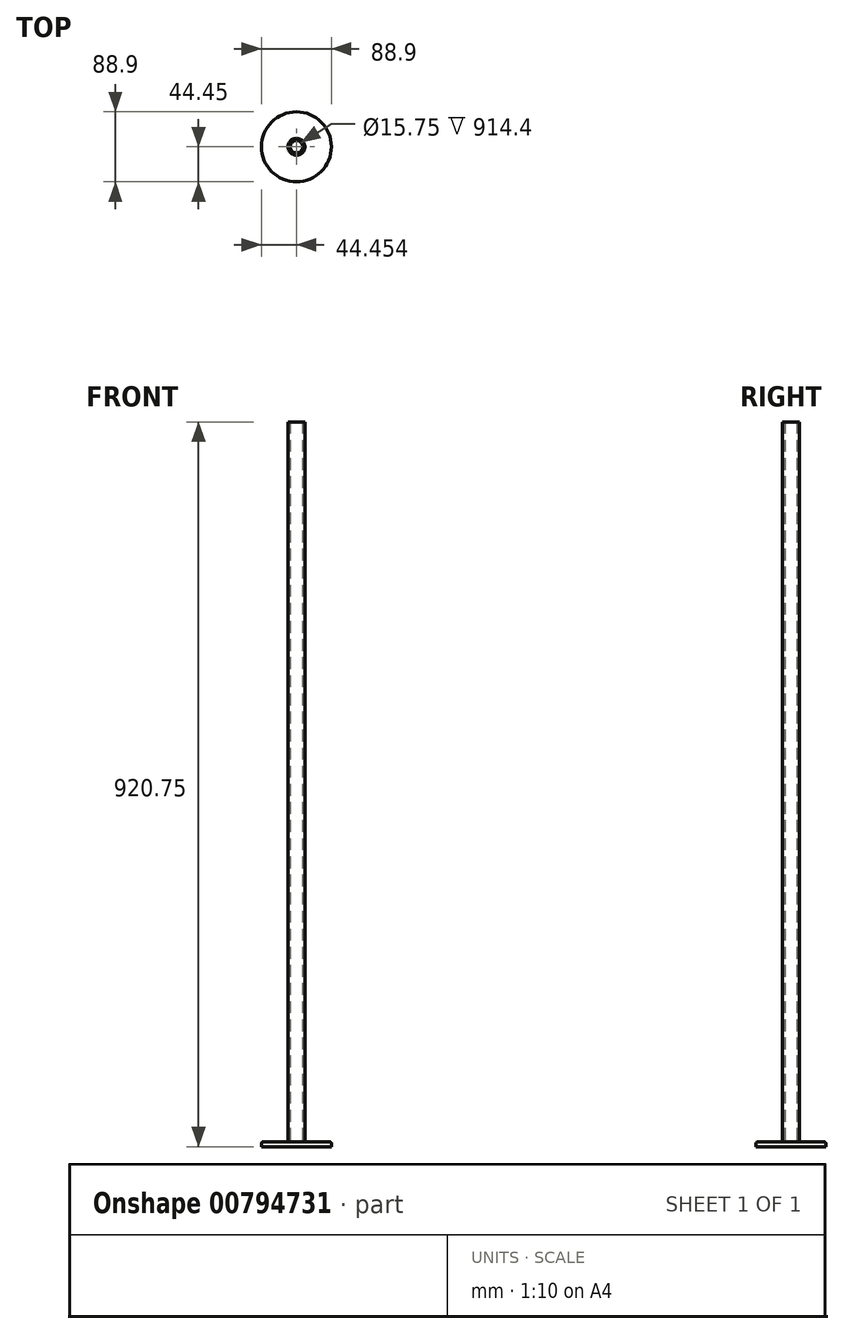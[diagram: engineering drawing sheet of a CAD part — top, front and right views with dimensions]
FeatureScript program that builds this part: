
annotation { "Feature Type Name" : "Feature", "Feature Type Description" : "" }
export const myFeature = defineFeature(function(context is Context, id is Id, definition is map)
    precondition{}
    {
        {
            var Q0;
            Q0=qCreatedBy(makeId("Top.planeOp"),FACE);
            var sketch = newSketch(context, id + "F0", { "sketchPlane" : qUnion([Q0])});
            skCircle(sketch, "E0", {"center": v(-10.73, -254) * mm, "radius": 44.45 * mm});
            skSolve(sketch);
        }
        {
            var Q0;
            Q0=qSketchRegion(id+"F0",true);
            extrude(context, id + "F1", {"entities" : qUnion([Q0]), "depth" : 6.35 * mm, "offsetDistance" : 25.4 * mm});
        }
        {
            var Q0;
            Q0=makeQuery(id+"F1.opExtrude","CAP_EDGE",EDGE,{"disambiguationData":[OSD([sQuery(id+"F0.wireOp",EDGE,"E0")])],"isStart":false});
            fillet(context, id + "F2", {"entities" : qUnion([Q0]), "radius" : 2.54 * mm, "tangentPropagation" : true, "allowEdgeOverflow" : false});
        }
        {
            var Q0;
            Q0=makeQuery(id+"F1.opExtrude","CAP_FACE",FACE,{"disambiguationData":[OSD([sQuery(id+"F0.wireOp",EDGE,"E0")])],"isStart":false});
            var sketch = newSketch(context, id + "F3", { "sketchPlane" : qUnion([Q0])});
            skCircle(sketch, "E1", {"center": v(-10.73, -254) * mm, "radius": 10.67 * mm});
            skCircle(sketch, "E2", {"center": v(-10.73, -254) * mm, "radius": 7.87 * mm});
            skSolve(sketch);
        }
        {
            var Q0;
            Q0=qSketchRegion(id+"F3",true);
            extrude(context, id + "F4", {"entities" : qUnion([Q0]), "depth" : 914.4 * mm, "offsetDistance" : 25.4 * mm});
        }
    });
